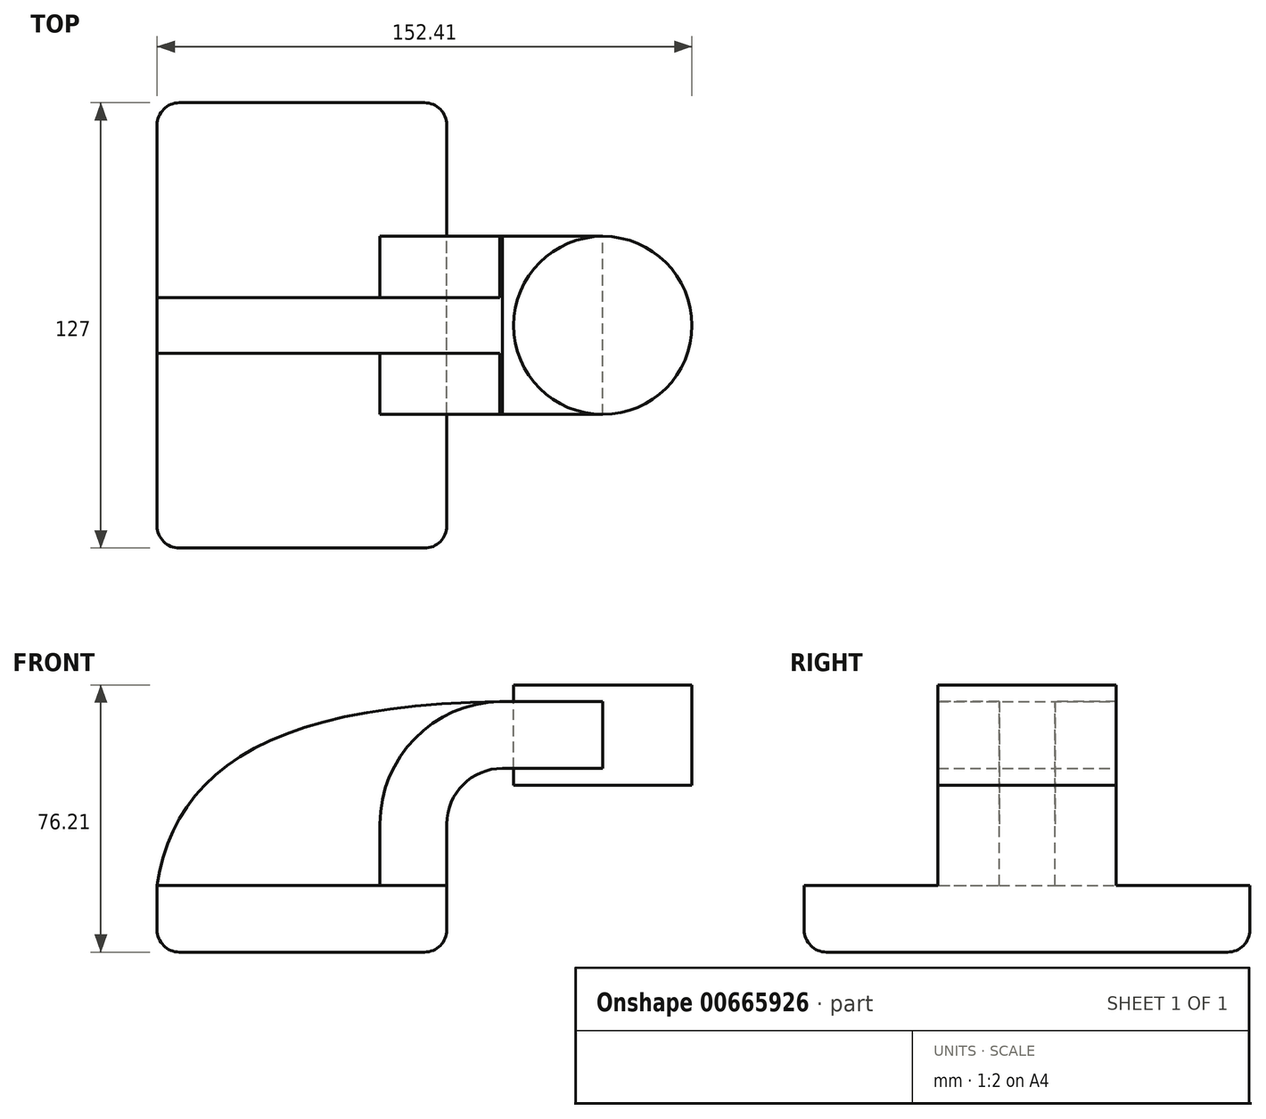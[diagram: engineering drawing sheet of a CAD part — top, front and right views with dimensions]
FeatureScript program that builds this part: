
annotation { "Feature Type Name" : "Feature", "Feature Type Description" : "" }
export const myFeature = defineFeature(function(context is Context, id is Id, definition is map)
    precondition{}
    {
        {
            var Q0;
            Q0=qCreatedBy(makeId("Front.planeOp"),FACE);
            var sketch = newSketch(context, id + "F0", { "sketchPlane" : qUnion([Q0])});
            skLineSegment(sketch, "E0.bottom", {"start": v(-41.28, 9.52) * mm, "end": v(41.28, 9.53) * mm});
            skLineSegment(sketch, "E0.top", {"start": v(-41.28, -9.53) * mm, "end": v(41.28, -9.53) * mm});
            skLineSegment(sketch, "E0.left", {"start": v(-41.28, 9.52) * mm, "end": v(-41.28, -9.53) * mm});
            skLineSegment(sketch, "E0.right", {"start": v(41.28, 9.53) * mm, "end": v(41.28, -9.52) * mm});
            skPoint(sketch, "E0.middle", {"position": v(0, 0) * mm});
            skLineSegment(sketch, "E1.bottom", {"start": v(111.12, 38.1) * mm, "end": v(60.32, 38.1) * mm});
            skLineSegment(sketch, "E1.top", {"start": v(111.12, 66.68) * mm, "end": v(60.32, 66.68) * mm});
            skLineSegment(sketch, "E1.left", {"start": v(111.12, 38.1) * mm, "end": v(111.12, 66.68) * mm});
            skLineSegment(sketch, "E1.right", {"start": v(60.32, 38.1) * mm, "end": v(60.32, 66.68) * mm});
            skPoint(sketch, "E1.middle", {"position": v(85.72, 52.39) * mm});
            skLineSegment(sketch, "E2", {"start": v(41.27, 9.53) * mm, "end": v(41.27, 27) * mm});
            skArc(sketch, "E3", {"start": v(41.27, 27) * mm, "mid": v(45.92, 38.23) * mm, "end": v(57.15, 42.88) * mm});
            skLineSegment(sketch, "E4", {"start": v(57.15, 42.88) * mm, "end": v(85.72, 42.88) * mm});
            skArc(sketch, "E5.0", {"start": v(22.22, 27) * mm, "mid": v(32.45, 51.7) * mm, "end": v(57.15, 61.93) * mm});
            skLineSegment(sketch, "E5.1", {"start": v(22.22, 9.53) * mm, "end": v(22.22, 27) * mm});
            skLineSegment(sketch, "E6", {"start": v(57.15, 61.93) * mm, "end": v(85.72, 61.93) * mm});
            skLineSegment(sketch, "E7", {"start": v(85.72, 61.93) * mm, "end": v(85.72, 42.88) * mm});
            skFitSpline(sketch, "E8", {"points": [v(-41.27, 9.53) * mm, v(57.15, 61.93) * mm], "startDerivative": vector(14.12, 95.96) * mm, "endDerivative": vector(201.7, 1.94) * mm});
            skLineSegment(sketch, "E9", {"start": v(85.72, 38.1) * mm, "end": v(85.72, 66.68) * mm});
            skSolve(sketch);
        }
        {
            var Q0;
            Q0=makeQuery(id+"F0.imprint","IMPRINT",FACE,{"disambiguationData":[TD([[makeQuery(id+"F0.imprint","IMPRINT",EDGE,{"derivedFrom":sQuery(id+"F0.wireOp",EDGE,"E0.top")}),1.0]])]});
            extrude(context, id + "F1", {"entities" : qUnion([Q0]), "endBound" : BoundingType.SYMMETRIC, "depth" : 127 * mm, "offsetDistance" : 25.4 * mm});
        }
        {
            var Q0;
            {var subQ1=sQuery(id+"F0.wireOp",EDGE,"E2");Q0=makeQuery(id+"F0.imprint","IMPRINT",FACE,{"disambiguationData":[TD([[makeQuery(id+"F0.imprint","IMPRINT",EDGE,{"derivedFrom":subQ1}),1.0]])]});}
            var Q1;
            {var subQ5=sQuery(id+"F0.wireOp",EDGE,"E7");Q1=makeQuery(id+"F0.imprint","IMPRINT",FACE,{"disambiguationData":[TD([[makeQuery(id+"F0.imprint","IMPRINT",EDGE,{"derivedFrom":subQ5}),-1.0]])]});}
            var Q2;
            {var subQ0=sQuery(id+"F0.wireOp",EDGE,"E4");var subQ1=sQuery(id+"F0.wireOp",EDGE,"E1.right");var subQ2=makeQuery(id+"F0.imprint","INTERSECT",VERTEX,{"derivedFrom":[subQ1,subQ0]});Q2=makeQuery(id+"F0.imprint","IMPRINT",FACE,{"disambiguationData":[TD([[makeQuery(id+"F0.imprint","IMPRINT",EDGE,{"disambiguationData":[TD([[subQ2,-1.0]])],"derivedFrom":subQ1}),-1.0]])]});}
            extrude(context, id + "F2", {"entities" : qUnion([Q0, Q1, Q2]), "operationType" : NewBodyOperationType.ADD, "endBound" : BoundingType.SYMMETRIC, "depth" : 50.8 * mm, "offsetDistance" : 25.4 * mm});
        }
        {
            var Q0;
            {var subQ3=sQuery(id+"F0.wireOp",EDGE,"E5.1");Q0=makeQuery(id+"F0.imprint","IMPRINT",FACE,{"disambiguationData":[TD([[makeQuery(id+"F0.imprint","IMPRINT",EDGE,{"derivedFrom":subQ3}),1.0]])]});}
            extrude(context, id + "F3", {"entities" : qUnion([Q0]), "operationType" : NewBodyOperationType.ADD, "endBound" : BoundingType.SYMMETRIC, "depth" : 15.88 * mm, "offsetDistance" : 25.4 * mm});
        }
        {
            var Q0;
            {var subQ4=sQuery(id+"F0.wireOp",EDGE,"E1.left");Q0=makeQuery(id+"F0.imprint","IMPRINT",FACE,{"disambiguationData":[TD([[makeQuery(id+"F0.imprint","IMPRINT",EDGE,{"derivedFrom":subQ4}),1.0]])]});}
            var Q1;
            Q1=sQuery(id+"F0.wireOp",EDGE,"E7");
            revolve(context, id + "F4", {"entities" : qUnion([Q0]), "axis" : qUnion([Q1]), "revolveType" : RevolveType.FULL});
        }
        {
            var Q0;
            Q0=makeQuery(id+"F1.opExtrude","CAP_EDGE",EDGE,{"disambiguationData":[OSD([sQuery(id+"F0.wireOp",EDGE,"E0.top")])],"isStart":false});
            var Q1;
            Q1=makeQuery(id+"F1.opExtrude","SWEPT_EDGE",EDGE,{"disambiguationData":[OSD([sQuery(id+"F0.wireOp",EDGE,"E0.top"),sQuery(id+"F0.wireOp",EDGE,"E0.right")])]});
            var Q2;
            Q2=makeQuery(id+"F1.opExtrude","CAP_EDGE",EDGE,{"disambiguationData":[OSD([sQuery(id+"F0.wireOp",EDGE,"E0.top")])],"isStart":true});
            var Q3;
            Q3=makeQuery(id+"F1.opExtrude","SWEPT_EDGE",EDGE,{"disambiguationData":[OSD([sQuery(id+"F0.wireOp",EDGE,"E0.top"),sQuery(id+"F0.wireOp",EDGE,"E0.left")])]});
            var Q4;
            Q4=makeQuery(id+"F1.opExtrude","CAP_EDGE",EDGE,{"disambiguationData":[OSD([sQuery(id+"F0.wireOp",EDGE,"E0.right")])],"isStart":true});
            var Q5;
            Q5=makeQuery(id+"F1.opExtrude","CAP_EDGE",EDGE,{"disambiguationData":[OSD([sQuery(id+"F0.wireOp",EDGE,"E0.left")])],"isStart":true});
            var Q6;
            Q6=makeQuery(id+"F1.opExtrude","CAP_EDGE",EDGE,{"disambiguationData":[OSD([sQuery(id+"F0.wireOp",EDGE,"E0.left")])],"isStart":false});
            var Q7;
            Q7=makeQuery(id+"F1.opExtrude","CAP_EDGE",EDGE,{"disambiguationData":[OSD([sQuery(id+"F0.wireOp",EDGE,"E0.right")])],"isStart":false});
            fillet(context, id + "F5", {"entities" : qUnion([Q0, Q1, Q2, Q3, Q4, Q5, Q6, Q7]), "radius" : 6.35 * mm, "tangentPropagation" : true, "allowEdgeOverflow" : false});
        }
    });
